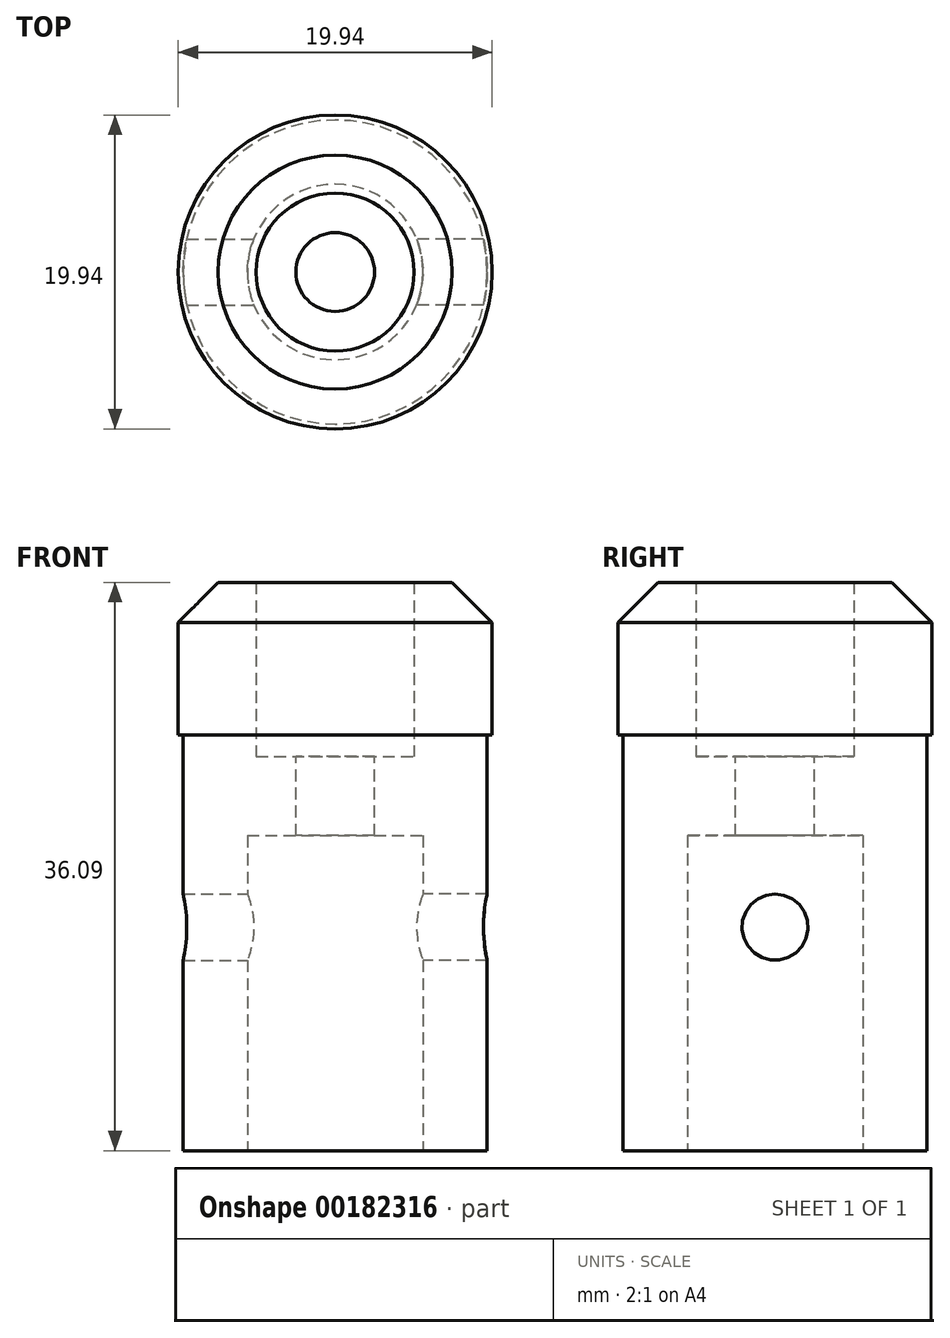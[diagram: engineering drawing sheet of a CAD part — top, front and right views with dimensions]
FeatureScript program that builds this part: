
annotation { "Feature Type Name" : "Feature", "Feature Type Description" : "" }
export const myFeature = defineFeature(function(context is Context, id is Id, definition is map)
    precondition{}
    {
        {
            var Q0;
            Q0=qCreatedBy(makeId("Front.planeOp"),FACE);
            var sketch = newSketch(context, id + "F0", { "sketchPlane" : qUnion([Q0])});
            skLineSegment(sketch, "E0", {"start": v(0, 0) * mm, "end": v(0, 36.1) * mm, "construction": true});
            skLineSegment(sketch, "E1", {"start": v(5.58, 0) * mm, "end": v(5.58, 20.02) * mm});
            skLineSegment(sketch, "E2", {"start": v(5.58, 20.02) * mm, "end": v(0, 20.02) * mm});
            skLineSegment(sketch, "E3", {"start": v(0, 20.02) * mm, "end": v(0, 25.04) * mm});
            skLineSegment(sketch, "E4", {"start": v(0, 25.04) * mm, "end": v(5.02, 25.04) * mm});
            skLineSegment(sketch, "E5", {"start": v(5.02, 25.04) * mm, "end": v(5.02, 36.1) * mm});
            skLineSegment(sketch, "E6", {"start": v(5.02, 36.1) * mm, "end": v(7.43, 36.1) * mm});
            skLineSegment(sketch, "E7", {"start": v(7.43, 36.1) * mm, "end": v(9.97, 33.55) * mm});
            skLineSegment(sketch, "E8", {"start": v(9.97, 33.55) * mm, "end": v(9.97, 26.42) * mm});
            skLineSegment(sketch, "E9", {"start": v(9.97, 26.42) * mm, "end": v(9.65, 26.42) * mm});
            skLineSegment(sketch, "E10", {"start": v(9.65, 26.42) * mm, "end": v(9.65, 0) * mm});
            skLineSegment(sketch, "E11", {"start": v(9.65, 0) * mm, "end": v(5.58, 0) * mm});
            skSolve(sketch);
        }
        {
            var Q0;
            Q0=makeQuery(id+"F0.imprint","IMPRINT",FACE,{"disambiguationData":[TD([[makeQuery(id+"F0.imprint","IMPRINT",EDGE,{"derivedFrom":sQuery(id+"F0.wireOp",EDGE,"E1")}),-1.0]])]});
            var Q1;
            Q1=sQuery(id+"F0.wireOp",EDGE,"E0");
            revolve(context, id + "F1", {"entities" : qUnion([Q0]), "axis" : qUnion([Q1]), "revolveType" : RevolveType.FULL});
        }
        {
            var Q0;
            Q0=makeQuery(id+"F1.opRevolve","SWEPT_FACE",FACE,{"disambiguationData":[OSD([sQuery(id+"F0.wireOp",EDGE,"E4")])]});
            var sketch = newSketch(context, id + "F2", { "sketchPlane" : qUnion([Q0])});
            skPoint(sketch, "E12", {"position": v(0, 0) * mm});
            skSolve(sketch);
        }
        {
            var Q0;
            Q0=qCreatedBy(makeId("Right.planeOp"),FACE);
            var sketch = newSketch(context, id + "F3", { "sketchPlane" : qUnion([Q0])});
            skCircle(sketch, "E13", {"center": v(0, 14.2) * mm, "radius": 2.05 * mm, "construction": true});
            skLineSegment(sketch, "E14", {"start": v(0, 0) * mm, "end": v(0, 12.15) * mm, "construction": true});
            skSolve(sketch);
        }
        {
            var Q0;
            Q0=sQuery(id+"F2.wireOp",VERTEX,"E12");
            var Q1;
            Q1=makeQuery(id+"F1.opRevolve","SWEPT_BODY",BODY,{"disambiguationData":[OSD([sQuery(id+"F0.wireOp",EDGE,"E1"),sQuery(id+"F0.wireOp",EDGE,"E2"),sQuery(id+"F0.wireOp",EDGE,"E3"),sQuery(id+"F0.wireOp",EDGE,"E4"),sQuery(id+"F0.wireOp",EDGE,"E5"),sQuery(id+"F0.wireOp",EDGE,"E6"),sQuery(id+"F0.wireOp",EDGE,"E7"),sQuery(id+"F0.wireOp",EDGE,"E8"),sQuery(id+"F0.wireOp",EDGE,"E9"),sQuery(id+"F0.wireOp",EDGE,"E10"),sQuery(id+"F0.wireOp",EDGE,"E11")])]});
            hole(context, id + "F4", {"style" : HoleStyle.SIMPLE, "endStyle" : HoleEndStyle.THROUGH, "standardTappedOrClearance" : lookupTablePath({ "standard" : "ISO", "engagement" : "75%", "pitch" : "1 mm", "size" : "M6", "type" : "Tapped" }), "standardBlindInLast" : lookupTablePath({ "standard" : "ISO", "engagement" : "75%", "pitch" : "1 mm", "size" : "M6", "type" : "Tapped" }), "holeDiameter" : 5 * mm, "locations" : qUnion([Q0]), "scope" : qUnion([Q1]), "isTappedThrough" : true, "majorDiameter" : 6 * mm, "showTappedDepth" : true});
        }
        {
            var Q0;
            Q0=sQuery(id+"F3.wireOp",VERTEX,"E13.center");
            var Q1;
            Q1=makeQuery(id+"F1.opRevolve","SWEPT_BODY",BODY,{"disambiguationData":[OSD([sQuery(id+"F0.wireOp",EDGE,"E1"),sQuery(id+"F0.wireOp",EDGE,"E2"),sQuery(id+"F0.wireOp",EDGE,"E3"),sQuery(id+"F0.wireOp",EDGE,"E4"),sQuery(id+"F0.wireOp",EDGE,"E5"),sQuery(id+"F0.wireOp",EDGE,"E6"),sQuery(id+"F0.wireOp",EDGE,"E7"),sQuery(id+"F0.wireOp",EDGE,"E8"),sQuery(id+"F0.wireOp",EDGE,"E9"),sQuery(id+"F0.wireOp",EDGE,"E10"),sQuery(id+"F0.wireOp",EDGE,"E11")])]});
            hole(context, id + "F5", {"style" : HoleStyle.SIMPLE, "endStyle" : HoleEndStyle.THROUGH, "standardTappedOrClearance" : lookupTablePath({ "standard" : "ISO", "engagement" : "75%", "pitch" : "0.8 mm", "size" : "M5", "type" : "Tapped" }), "standardBlindInLast" : lookupTablePath({ "standard" : "ISO", "engagement" : "75%", "pitch" : "0.8 mm", "size" : "M5", "type" : "Tapped" }), "holeDiameter" : 4.2 * mm, "locations" : qUnion([Q0]), "scope" : qUnion([Q1]), "isTappedThrough" : true, "majorDiameter" : 5 * mm, "showTappedDepth" : true});
        }
        {
            var Q0;
            Q0=sQuery(id+"F3.wireOp",VERTEX,"E13.center");
            var Q1;
            Q1=makeQuery(id+"F1.opRevolve","SWEPT_BODY",BODY,{"disambiguationData":[OSD([sQuery(id+"F0.wireOp",EDGE,"E1"),sQuery(id+"F0.wireOp",EDGE,"E2"),sQuery(id+"F0.wireOp",EDGE,"E3"),sQuery(id+"F0.wireOp",EDGE,"E4"),sQuery(id+"F0.wireOp",EDGE,"E5"),sQuery(id+"F0.wireOp",EDGE,"E6"),sQuery(id+"F0.wireOp",EDGE,"E7"),sQuery(id+"F0.wireOp",EDGE,"E8"),sQuery(id+"F0.wireOp",EDGE,"E9"),sQuery(id+"F0.wireOp",EDGE,"E10"),sQuery(id+"F0.wireOp",EDGE,"E11")])]});
            hole(context, id + "F6", {"style" : HoleStyle.SIMPLE, "endStyle" : HoleEndStyle.THROUGH, "oppositeDirection" : true, "standardTappedOrClearance" : lookupTablePath({ "standard" : "ISO", "engagement" : "75%", "pitch" : "0.8 mm", "size" : "M5", "type" : "Tapped" }), "standardBlindInLast" : lookupTablePath({ "standard" : "ISO", "engagement" : "75%", "pitch" : "0.8 mm", "size" : "M5", "type" : "Tapped" }), "holeDiameter" : 4.2 * mm, "locations" : qUnion([Q0]), "scope" : qUnion([Q1]), "isTappedThrough" : true, "majorDiameter" : 5 * mm, "showTappedDepth" : true});
        }
    });
